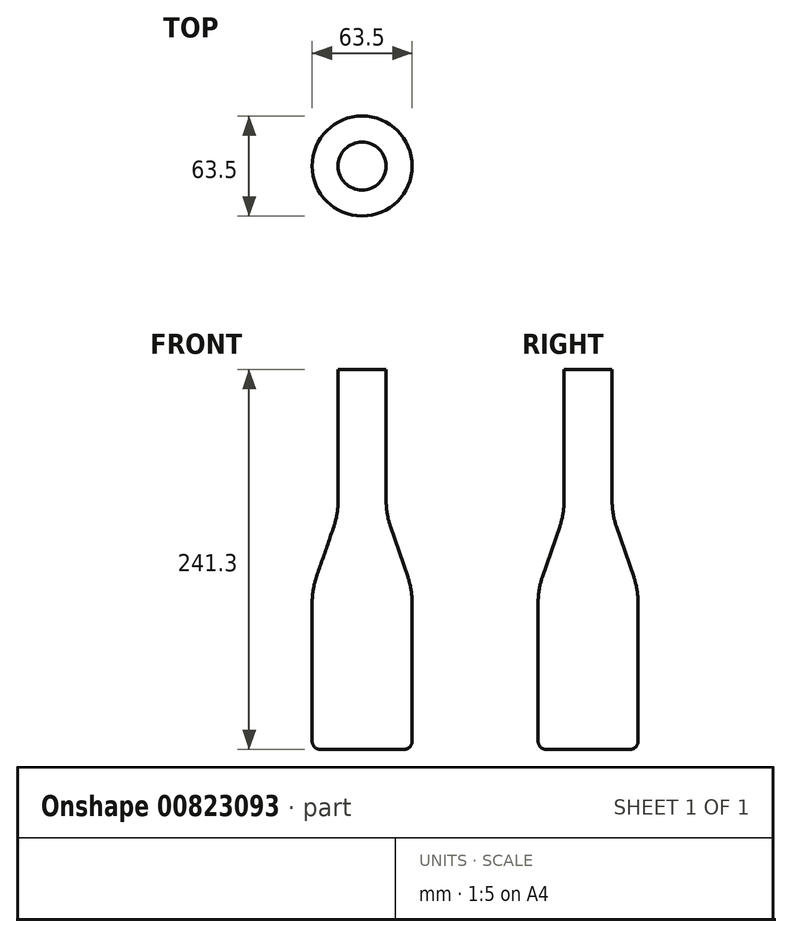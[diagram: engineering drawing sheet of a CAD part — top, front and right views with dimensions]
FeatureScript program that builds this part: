
annotation { "Feature Type Name" : "Feature", "Feature Type Description" : "" }
export const myFeature = defineFeature(function(context is Context, id is Id, definition is map)
    precondition{}
    {
        {
            var Q0;
            Q0=qCreatedBy(makeId("Front.planeOp"),FACE);
            var sketch = newSketch(context, id + "F0", { "sketchPlane" : qUnion([Q0])});
            skLineSegment(sketch, "E0", {"start": v(0, 120.65) * mm, "end": v(0, -120.65) * mm});
            skLineSegment(sketch, "E1", {"start": v(0, -120.65) * mm, "end": v(31.75, -120.65) * mm});
            skLineSegment(sketch, "E2", {"start": v(31.75, -120.65) * mm, "end": v(31.75, -19.05) * mm});
            skLineSegment(sketch, "E3", {"start": v(31.75, -19.05) * mm, "end": v(15.24, 28.96) * mm});
            skLineSegment(sketch, "E4", {"start": v(15.24, 28.96) * mm, "end": v(15.24, 120.65) * mm});
            skLineSegment(sketch, "E5", {"start": v(15.24, 120.65) * mm, "end": v(0, 120.65) * mm});
            skLineSegment(sketch, "E6", {"start": v(0, 149.97) * mm, "end": v(0, -145.34) * mm, "construction": true});
            skSolve(sketch);
        }
        {
            var Q0;
            Q0 = qSketchRegion(id + "F0", true);
            var Q1;
            Q1=sQuery(id+"F0.wireOp",EDGE,"E6");
            revolve(context, id + "F1", {"surfaceOperationType" : NewSurfaceOperationType.NEW, "entities" : qUnion([Q0]), "axis" : qUnion([Q1]), "revolveType" : RevolveType.FULL});
        }
        {
            var Q0;
            Q0=makeQuery(id+"F1.opRevolve","SWEPT_EDGE",EDGE,{"disambiguationData":[OSD([sQuery(id+"F0.wireOp",EDGE,"E1"),sQuery(id+"F0.wireOp",EDGE,"E2")])]});
            fillet(context, id + "F2", {"entities" : qUnion([Q0]), "radius" : 5.08 * mm, "tangentPropagation" : true, "allowEdgeOverflow" : false});
        }
        {
            var Q0;
            Q0=makeQuery(id+"F1.opRevolve","SWEPT_EDGE",EDGE,{"disambiguationData":[OSD([sQuery(id+"F0.wireOp",EDGE,"E2"),sQuery(id+"F0.wireOp",EDGE,"E3")])]});
            var Q1;
            Q1=makeQuery(id+"F1.opRevolve","SWEPT_EDGE",EDGE,{"disambiguationData":[OSD([sQuery(id+"F0.wireOp",EDGE,"E3"),sQuery(id+"F0.wireOp",EDGE,"E4")])]});
            fillet(context, id + "F3", {"entities" : qUnion([Q0, Q1]), "radius" : 50.8 * mm, "tangentPropagation" : true, "allowEdgeOverflow" : false});
        }
    });
